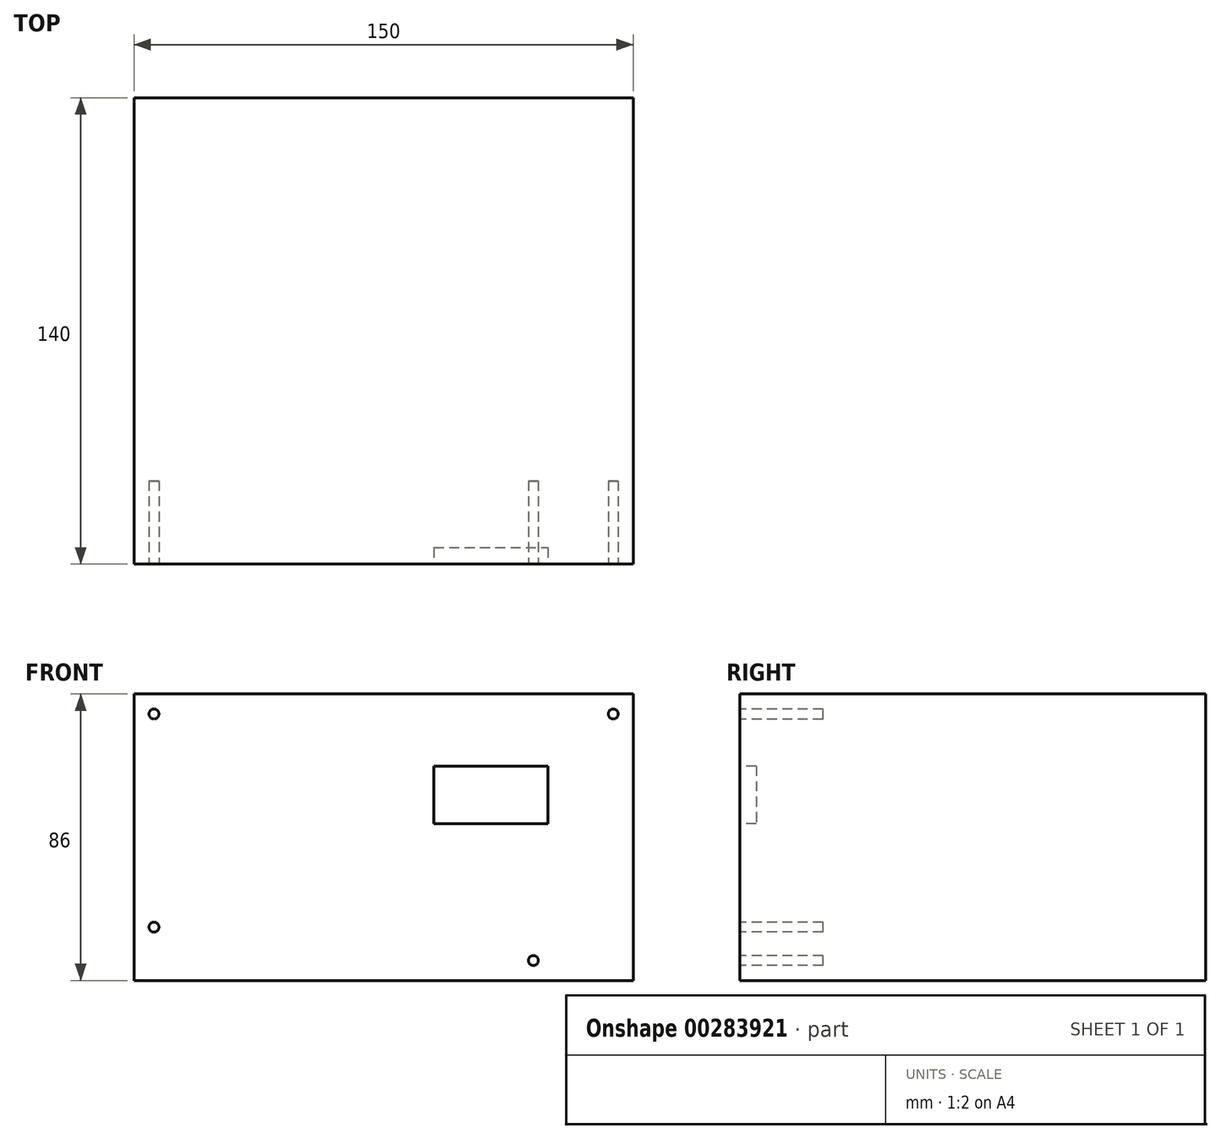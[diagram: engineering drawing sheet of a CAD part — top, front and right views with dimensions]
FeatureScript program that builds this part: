
annotation { "Feature Type Name" : "Feature", "Feature Type Description" : "" }
export const myFeature = defineFeature(function(context is Context, id is Id, definition is map)
    precondition{}
    {
        {
            var Q0;
            Q0=qCreatedBy(makeId("Top.planeOp"),FACE);
            var sketch = newSketch(context, id + "F0", { "sketchPlane" : qUnion([Q0])});
            skLineSegment(sketch, "E0.bottom", {"start": v(75, -70) * mm, "end": v(-75, -70) * mm});
            skLineSegment(sketch, "E0.top", {"start": v(75, 70) * mm, "end": v(-75, 70) * mm});
            skLineSegment(sketch, "E0.left", {"start": v(75, -70) * mm, "end": v(75, 70) * mm});
            skLineSegment(sketch, "E0.right", {"start": v(-75, -70) * mm, "end": v(-75, 70) * mm});
            skPoint(sketch, "E0.middle", {"position": v(0, 0) * mm});
            skSolve(sketch);
        }
        {
            var Q0;
            Q0 = qSketchRegion(id + "F0", true);
            extrude(context, id + "F1", {"entities" : qUnion([Q0]), "endBound" : BoundingType.SYMMETRIC, "depth" : 86 * mm});
        }
        {
            var Q0;
            Q0=makeQuery(id+"F1.opExtrude","SWEPT_FACE",FACE,{"disambiguationData":[OSD([sQuery(id+"F0.wireOp",EDGE,"E0.bottom")])]});
            var sketch = newSketch(context, id + "F2", { "sketchPlane" : qUnion([Q0])});
            skCircle(sketch, "E1", {"center": v(-69, 37) * mm, "radius": 1.5 * mm});
            skCircle(sketch, "E2", {"center": v(69, 37) * mm, "radius": 1.5 * mm});
            skCircle(sketch, "E3", {"center": v(45, -37) * mm, "radius": 1.5 * mm});
            skCircle(sketch, "E4", {"center": v(-69, -27) * mm, "radius": 1.5 * mm});
            skSolve(sketch);
        }
        {
            var Q0;
            Q0 = qSketchRegion(id + "F2", true);
            extrude(context, id + "F3", {"entities" : qUnion([Q0]), "operationType" : NewBodyOperationType.REMOVE, "oppositeDirection" : true, "depth" : 25 * mm});
        }
        {
            var Q0;
            Q0=makeQuery(id+"F1.opExtrude","SWEPT_FACE",FACE,{"disambiguationData":[OSD([sQuery(id+"F0.wireOp",EDGE,"E0.bottom")])]});
            var sketch = newSketch(context, id + "F4", { "sketchPlane" : qUnion([Q0])});
            skLineSegment(sketch, "E5.bottom", {"start": v(15.15, 21.39) * mm, "end": v(49.4, 21.39) * mm});
            skLineSegment(sketch, "E5.top", {"start": v(15.15, 4.03) * mm, "end": v(49.4, 4.03) * mm});
            skLineSegment(sketch, "E5.left", {"start": v(15.15, 21.39) * mm, "end": v(15.15, 4.03) * mm});
            skLineSegment(sketch, "E5.right", {"start": v(49.4, 21.39) * mm, "end": v(49.4, 4.03) * mm});
            skSolve(sketch);
        }
        {
            var Q0;
            Q0 = qSketchRegion(id + "F4", true);
            extrude(context, id + "F5", {"entities" : qUnion([Q0]), "operationType" : NewBodyOperationType.REMOVE, "oppositeDirection" : true, "depth" : 5 * mm});
        }
    });
